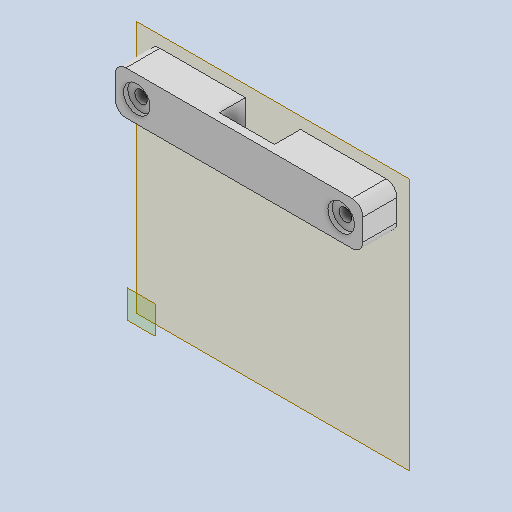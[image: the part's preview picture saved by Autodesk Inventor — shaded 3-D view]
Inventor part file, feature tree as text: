
AUTODESK INVENTOR PART (.ipt)
format: ipt  version: 2023 (Build 270158000, 158)  size: 131,584 bytes
history: native  units: mm
features: reference x6, other x4, extrude x3, sketch x3, plane x2, projected_geometry x1
ambient origin geometry x8: Origin, YZ Plane, XZ Plane, XY Plane, X Axis, Y Axis, Z Axis, Center Point
bodies: Solid1 (feature_tree)
feature tree (19):
  plane  "Work Plane1"
  extrude  "Extrusion1"  Depth=7.842mm
  extrude  "Extrusion2"  Depth=0.175mm
  plane  "Work Plane2"
  extrude  "Extrusion3"  Depth=12.908mm TaperAngle=0.0deg
  sketch  "Sketch1"  dims[d0=7.842mm d1=0.0mm d2=0.1mm]
  reference  "Reference1"
  reference  "Reference2"
  reference  "Reference3"
  sketch  "Sketch2"  dims[d3=0.1mm d4=0.175mm]
  sketch  "Sketch3"  dims[d5=12.908mm d6=0.0mm d7=12.908mm d8=0.0mm]
  projected_geometry  "Projected Loop1"
  reference  "Reference4"
  reference  "Reference5"
  reference  "Reference6"
  parser-record x1  (decoder bookkeeping rows leaked as tree rows — omitted from the tree; the rows remain in map.json)
  other  "Assembly_V6.iam"
  other  "house_V6:1"
  other  "longerScrew:1"
note: 1 file-system path scrubbed to <path> (originals preserved in map.json)
